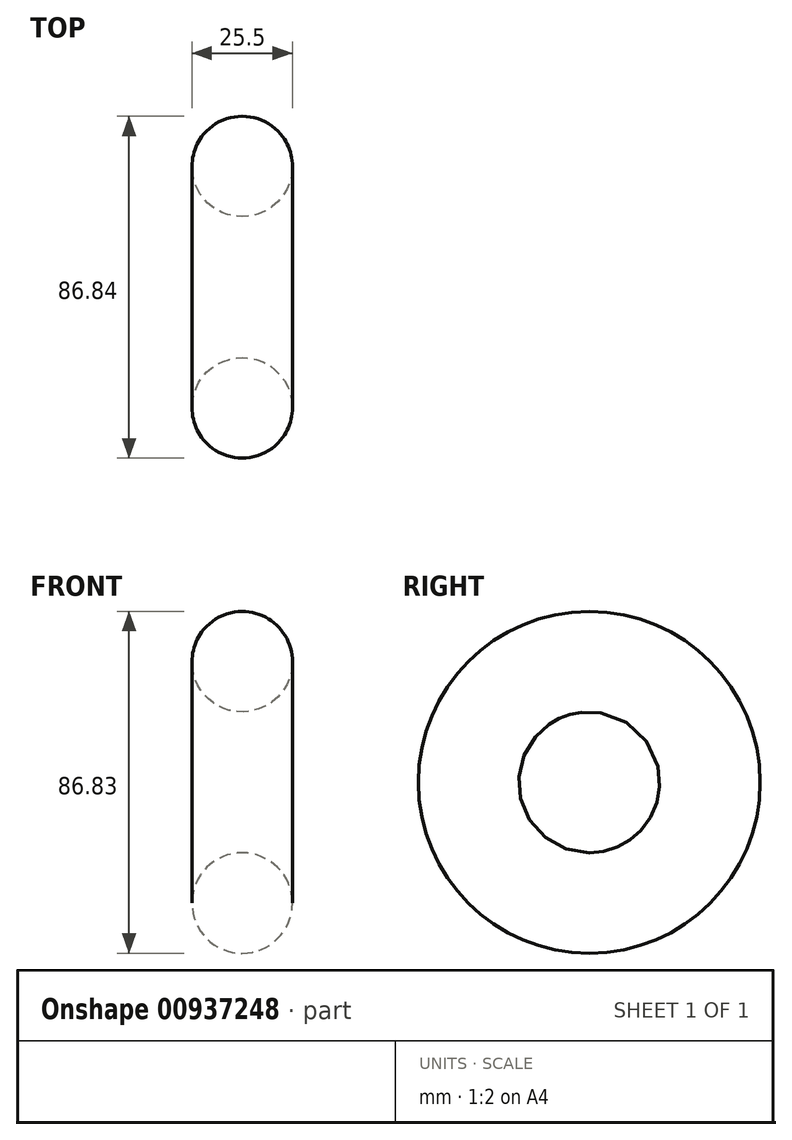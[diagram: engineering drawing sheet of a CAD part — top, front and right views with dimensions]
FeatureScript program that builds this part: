
annotation { "Feature Type Name" : "Feature", "Feature Type Description" : "" }
export const myFeature = defineFeature(function(context is Context, id is Id, definition is map)
    precondition{}
    {
        {
            var Q0;
            Q0=qCreatedBy(makeId("Front.planeOp"),FACE);
            var sketch = newSketch(context, id + "F0", { "sketchPlane" : qUnion([Q0])});
            skCircle(sketch, "E0", {"center": v(0, 0) * mm, "radius": 12.75 * mm});
            skLineSegment(sketch, "E1", {"start": v(37.25, -30.66) * mm, "end": v(-19.73, -30.66) * mm});
            skSolve(sketch);
        }
        {
            var Q0;
            Q0=makeQuery(id+"F0.imprint","IMPRINT",FACE,{"disambiguationData":[TD([[makeQuery(id+"F0.imprint","IMPRINT",EDGE,{"derivedFrom":sQuery(id+"F0.wireOp",EDGE,"E0")}),1.0]])]});
            var Q1;
            Q1=sQuery(id+"F0.wireOp",EDGE,"E0");
            var Q2;
            Q2=sQuery(id+"F0.wireOp",EDGE,"E1");
            revolve(context, id + "F1", {"bodyType" : ToolBodyType.SURFACE, "operationType" : NewBodyOperationType.INTERSECT, "surfaceOperationType" : NewSurfaceOperationType.NEW, "entities" : qUnion([Q0]), "surfaceEntities" : qUnion([Q1]), "axis" : qUnion([Q2]), "revolveType" : RevolveType.FULL, "oppositeDirection" : true});
        }
    });
